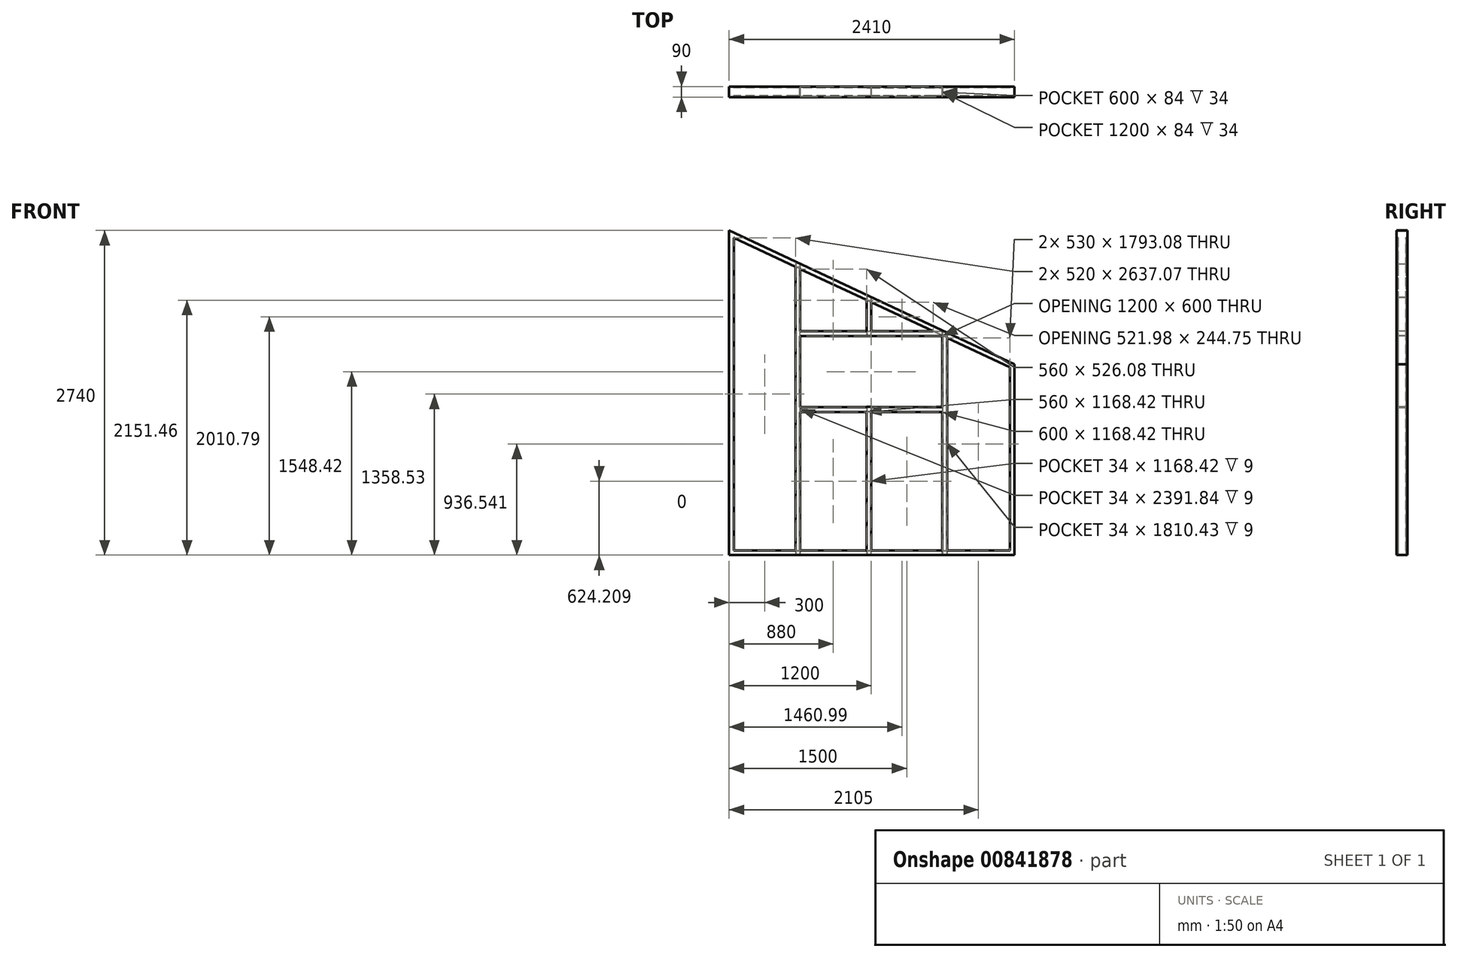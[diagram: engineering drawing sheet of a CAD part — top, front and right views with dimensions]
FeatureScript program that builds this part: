
annotation { "Feature Type Name" : "Feature", "Feature Type Description" : "" }
export const myFeature = defineFeature(function(context is Context, id is Id, definition is map)
    precondition{}
    {
        {
            var Q0;
            Q0=qCreatedBy(makeId("Front.planeOp"),FACE);
            var sketch = newSketch(context, id + "F0", { "sketchPlane" : qUnion([Q0])});
            skLineSegment(sketch, "E0", {"start": v(0, 0) * mm, "end": v(2410, 0) * mm});
            skLineSegment(sketch, "E1", {"start": v(2410, 0) * mm, "end": v(2410, 1610) * mm});
            skLineSegment(sketch, "E2", {"start": v(2410, 1610) * mm, "end": v(0, 2740) * mm});
            skLineSegment(sketch, "E3", {"start": v(0, 2740) * mm, "end": v(0, 0) * mm});
            skSolve(sketch);
        }
        {
            var Q0;
            Q0=qCreatedBy(makeId("Right.planeOp"),FACE);
            var sketch = newSketch(context, id + "F1", { "sketchPlane" : qUnion([Q0])});
            skLineSegment(sketch, "E4", {"start": v(0, 0) * mm, "end": v(-45, 0) * mm});
            skLineSegment(sketch, "E5", {"start": v(-45, 0) * mm, "end": v(-45, 40) * mm});
            skLineSegment(sketch, "E6", {"start": v(-45, 40) * mm, "end": v(-33, 40) * mm});
            skLineSegment(sketch, "E7.MirrorCS", {"start": v(45, 40) * mm, "end": v(33, 40) * mm});
            skLineSegment(sketch, "E8.MirrorCS", {"start": v(45, 0) * mm, "end": v(45, 40) * mm});
            skLineSegment(sketch, "E9.MirrorCS", {"start": v(0, 0) * mm, "end": v(45, 0) * mm});
            skLineSegment(sketch, "E10.0", {"start": v(-42, 37) * mm, "end": v(-33, 37) * mm});
            skLineSegment(sketch, "E10.1", {"start": v(-42, 3) * mm, "end": v(-42, 37) * mm});
            skLineSegment(sketch, "E10.2", {"start": v(42, 37) * mm, "end": v(33, 37) * mm});
            skLineSegment(sketch, "E10.3", {"start": v(42, 3) * mm, "end": v(42, 37) * mm});
            skLineSegment(sketch, "E10.4", {"start": v(0, 3) * mm, "end": v(42, 3) * mm});
            skLineSegment(sketch, "E10.5", {"start": v(0, 3) * mm, "end": v(-42, 3) * mm});
            skLineSegment(sketch, "E11", {"start": v(-33, 40) * mm, "end": v(-33, 37) * mm});
            skLineSegment(sketch, "E12", {"start": v(33, 40) * mm, "end": v(33, 37) * mm});
            skSolve(sketch);
        }
        {
            var Q0;
            Q0=makeQuery(id+"F1.imprint","IMPRINT",FACE,{"disambiguationData":[TD([[makeQuery(id+"F1.imprint","IMPRINT",EDGE,{"derivedFrom":sQuery(id+"F1.wireOp",EDGE,"E4")}),-1.0]])]});
            var Q1;
            Q1=sQuery(id+"F0.wireOp",EDGE,"E0");
            var Q2;
            Q2=sQuery(id+"F0.wireOp",EDGE,"E1");
            var Q3;
            Q3=sQuery(id+"F0.wireOp",EDGE,"E2");
            var Q4;
            Q4=sQuery(id+"F0.wireOp",EDGE,"E3");
            sweep(context, id + "F2", {"profiles" : qUnion([Q0]), "path" : qUnion([Q1, Q2, Q3, Q4])});
        }
        {
            var Q0;
            Q0=qCreatedBy(makeId("Front.planeOp"),FACE);
            var sketch = newSketch(context, id + "F3", { "sketchPlane" : qUnion([Q0])});
            skLineSegment(sketch, "E13", {"start": v(600, 0) * mm, "end": v(600, 2458.67) * mm});
            skLineSegment(sketch, "E14", {"start": v(1200, 0) * mm, "end": v(1200, 1251.84) * mm});
            skLineSegment(sketch, "E15", {"start": v(1800, 0) * mm, "end": v(1800, 1896.02) * mm});
            skLineSegment(sketch, "E16", {"start": v(1800, 1851.84) * mm, "end": v(600, 1851.84) * mm});
            skLineSegment(sketch, "E17", {"start": v(1800, 1251.84) * mm, "end": v(600, 1251.84) * mm});
            skLineSegment(sketch, "E18.trimOffspring", {"start": v(1200, 1851.84) * mm, "end": v(1200, 2177.34) * mm});
            skSolve(sketch);
        }
        {
            var Q0;
            Q0=makeQuery(id+"F2.opSweep","SWEPT_FACE",FACE,{"disambiguationData":[OSD([sQuery(id+"F0.wireOp",EDGE,"E0"),sQuery(id+"F1.wireOp",EDGE,"E4"),sQuery(id+"F1.wireOp",EDGE,"E9.MirrorCS")])]});
            var sketch = newSketch(context, id + "F4", { "sketchPlane" : qUnion([Q0])});
            skLineSegment(sketch, "E19", {"start": v(600, 0) * mm, "end": v(600, 45) * mm});
            skLineSegment(sketch, "E20", {"start": v(600, 45) * mm, "end": v(560, 45) * mm});
            skLineSegment(sketch, "E21", {"start": v(560, 45) * mm, "end": v(560, 33) * mm});
            skLineSegment(sketch, "E22.MirrorCS", {"start": v(600, 0) * mm, "end": v(600, -45) * mm});
            skLineSegment(sketch, "E23.MirrorCS", {"start": v(600, -45) * mm, "end": v(560, -45) * mm});
            skLineSegment(sketch, "E24.MirrorCS", {"start": v(560, -45) * mm, "end": v(560, -33) * mm});
            skLineSegment(sketch, "E25.0", {"start": v(563, -42) * mm, "end": v(563, -33) * mm});
            skLineSegment(sketch, "E25.1", {"start": v(597, -42) * mm, "end": v(563, -42) * mm});
            skLineSegment(sketch, "E25.2", {"start": v(563, 42) * mm, "end": v(563, 33) * mm});
            skLineSegment(sketch, "E25.3", {"start": v(597, 42) * mm, "end": v(563, 42) * mm});
            skLineSegment(sketch, "E25.4", {"start": v(597, 0) * mm, "end": v(597, 42) * mm});
            skLineSegment(sketch, "E25.5", {"start": v(597, 0) * mm, "end": v(597, -42) * mm});
            skLineSegment(sketch, "E26", {"start": v(560, 33) * mm, "end": v(563, 33) * mm});
            skLineSegment(sketch, "E27", {"start": v(560, -33) * mm, "end": v(563, -33) * mm});
            skLineSegment(sketch, "E28.1.0.0", {"start": v(1200, 45) * mm, "end": v(1160, 45) * mm});
            skLineSegment(sketch, "E28.1.0.1", {"start": v(1197, 42) * mm, "end": v(1163, 42) * mm});
            skLineSegment(sketch, "E28.1.0.2", {"start": v(1197, 0) * mm, "end": v(1197, -42) * mm});
            skLineSegment(sketch, "E28.1.0.3", {"start": v(1200, 0) * mm, "end": v(1200, 45) * mm});
            skLineSegment(sketch, "E28.1.0.4", {"start": v(1197, -42) * mm, "end": v(1163, -42) * mm});
            skLineSegment(sketch, "E28.1.0.5", {"start": v(1200, 0) * mm, "end": v(1200, -45) * mm});
            skLineSegment(sketch, "E28.1.0.6", {"start": v(1200, -45) * mm, "end": v(1160, -45) * mm});
            skLineSegment(sketch, "E28.1.0.7", {"start": v(1197, 0) * mm, "end": v(1197, 42) * mm});
            skLineSegment(sketch, "E28.1.0.8", {"start": v(1160, -45) * mm, "end": v(1160, -33) * mm});
            skLineSegment(sketch, "E28.1.0.9", {"start": v(1160, 33) * mm, "end": v(1163, 33) * mm});
            skLineSegment(sketch, "E28.1.0.10", {"start": v(1160, 45) * mm, "end": v(1160, 33) * mm});
            skLineSegment(sketch, "E28.1.0.11", {"start": v(1163, 42) * mm, "end": v(1163, 33) * mm});
            skLineSegment(sketch, "E28.1.0.12", {"start": v(1160, -33) * mm, "end": v(1163, -33) * mm});
            skLineSegment(sketch, "E28.1.0.13", {"start": v(1163, -42) * mm, "end": v(1163, -33) * mm});
            skLineSegment(sketch, "E28.2.0.3", {"start": v(1800, 0) * mm, "end": v(1800, 45) * mm});
            skLineSegment(sketch, "E28.2.0.5", {"start": v(1800, 0) * mm, "end": v(1800, -45) * mm});
            skLineSegment(sketch, "E28.direction1", {"start": v(560, -45) * mm, "end": v(1160, -45) * mm, "construction": true});
            skLineSegment(sketch, "E29.MirrorCS", {"start": v(1803, 0) * mm, "end": v(1803, -42) * mm});
            skLineSegment(sketch, "E30.MirrorCS", {"start": v(1803, -42) * mm, "end": v(1837, -42) * mm});
            skLineSegment(sketch, "E31.MirrorCS", {"start": v(1800, -45) * mm, "end": v(1840, -45) * mm});
            skLineSegment(sketch, "E32.MirrorCS", {"start": v(1840, -45) * mm, "end": v(1840, -33) * mm});
            skLineSegment(sketch, "E33.MirrorCS", {"start": v(1837, -42) * mm, "end": v(1837, -33) * mm});
            skLineSegment(sketch, "E34.MirrorCS", {"start": v(1840, -33) * mm, "end": v(1837, -33) * mm});
            skLineSegment(sketch, "E35.MirrorCS", {"start": v(1803, 0) * mm, "end": v(1803, 42) * mm});
            skLineSegment(sketch, "E36.MirrorCS", {"start": v(1803, 42) * mm, "end": v(1837, 42) * mm});
            skLineSegment(sketch, "E37.MirrorCS", {"start": v(1800, 45) * mm, "end": v(1840, 45) * mm});
            skLineSegment(sketch, "E38.MirrorCS", {"start": v(1837, 42) * mm, "end": v(1837, 33) * mm});
            skLineSegment(sketch, "E39.MirrorCS", {"start": v(1840, 45) * mm, "end": v(1840, 33) * mm});
            skLineSegment(sketch, "E40.MirrorCS", {"start": v(1840, 33) * mm, "end": v(1837, 33) * mm});
            skPoint(sketch, "E28.2.0.10.start.orphan", {"position": v(1760, 45) * mm});
            skPoint(sketch, "E28.2.0.11.start.orphan", {"position": v(1763, 42) * mm});
            skPoint(sketch, "E28.2.0.7.end.orphan", {"position": v(1797, 42) * mm});
            skPoint(sketch, "E28.2.0.2.start.orphan", {"position": v(1797, 0) * mm});
            skPoint(sketch, "E28.2.0.4.start.orphan", {"position": v(1797, -42) * mm});
            skPoint(sketch, "E28.2.0.6.end.orphan", {"position": v(1760, -45) * mm});
            skPoint(sketch, "E28.2.0.6.start.orphan", {"position": v(1800, -45) * mm});
            skPoint(sketch, "E28.2.0.13.start.orphan", {"position": v(1763, -42) * mm});
            skPoint(sketch, "E28.2.0.8.start.orphan", {"position": v(1760, -45) * mm});
            skPoint(sketch, "E28.2.0.12.end.orphan", {"position": v(1763, -33) * mm});
            skPoint(sketch, "E28.2.0.12.start.orphan", {"position": v(1760, -33) * mm});
            skPoint(sketch, "E28.2.0.9.end.orphan", {"position": v(1763, 33) * mm});
            skPoint(sketch, "E28.2.0.9.start.orphan", {"position": v(1760, 33) * mm});
            skSolve(sketch);
        }
        {
            var Q0;
            Q0 = qSketchRegion(id + "F4", true);
            var Q1;
            Q1=makeQuery(id+"F2.opSweep","SWEPT_FACE",FACE,{"disambiguationData":[OSD([sQuery(id+"F0.wireOp",EDGE,"E2"),sQuery(id+"F1.wireOp",EDGE,"E10.4"),sQuery(id+"F1.wireOp",EDGE,"E10.5")])]});
            extrude(context, id + "F5", {"entities" : qUnion([Q0]), "operationType" : NewBodyOperationType.ADD, "endBound" : BoundingType.UP_TO_SURFACE, "oppositeDirection" : true, "depth" : 25 * mm, "endBoundEntityFace" : qUnion([Q1]), "offsetDistance" : 25 * mm});
        }
        {
            var Q0;
            {var subQ0=sQuery(id+"F3.wireOp",EDGE,"E16");var subQ3=makeQuery(id+"F3.imprint","IMPRINT",VERTEX,{"derivedFrom":subQ0});Q0=makeQuery(id+"F3.imprint","IMPRINT",FACE,{"disambiguationData":[TD([[makeQuery(id+"F3.imprint","IMPRINT",EDGE,{"disambiguationData":[TD([[subQ3,1.0]])],"derivedFrom":subQ0}),1.0]])]});}
            var Q1;
            Q1=sQuery(id+"F3.wireOp",EDGE,"E16");
            var Q2;
            Q2=sQuery(id+"F3.wireOp",EDGE,"E17");
            extrude(context, id + "F6", {"entities" : qUnion([Q0]), "operationType" : NewBodyOperationType.REMOVE, "surfaceEntities" : qUnion([Q1, Q2]), "endBound" : BoundingType.THROUGH_ALL, "oppositeDirection" : true, "depth" : 25 * mm, "offsetDistance" : 25 * mm, "hasSecondDirection" : true, "secondDirectionBound" : SecondDirectionBoundingType.THROUGH_ALL, "secondDirectionOppositeDirection" : false, "secondDirectionDepth" : 25 * mm});
        }
        {
            var Q0;
            Q0=makeQuery(id+"F5.opExtrude","SWEPT_FACE",FACE,{"disambiguationData":[OSD([sQuery(id+"F4.wireOp",EDGE,"E19"),sQuery(id+"F4.wireOp",EDGE,"E22.MirrorCS")])]});
            var sketch = newSketch(context, id + "F7", { "sketchPlane" : qUnion([Q0])});
            skLineSegment(sketch, "E41", {"start": v(0, 1248.42) * mm, "end": v(45, 1248.42) * mm});
            skLineSegment(sketch, "E42", {"start": v(45, 1248.42) * mm, "end": v(45, 1208.42) * mm});
            skLineSegment(sketch, "E43", {"start": v(45, 1208.42) * mm, "end": v(33, 1208.42) * mm});
            skLineSegment(sketch, "E44.MirrorCS", {"start": v(0, 1248.42) * mm, "end": v(-45, 1248.42) * mm});
            skLineSegment(sketch, "E45.MirrorCS", {"start": v(-45, 1248.42) * mm, "end": v(-45, 1208.42) * mm});
            skLineSegment(sketch, "E46.MirrorCS", {"start": v(-45, 1208.42) * mm, "end": v(-33, 1208.42) * mm});
            skLineSegment(sketch, "E47.0", {"start": v(42, 1211.42) * mm, "end": v(33, 1211.42) * mm});
            skLineSegment(sketch, "E47.1", {"start": v(42, 1245.42) * mm, "end": v(42, 1211.42) * mm});
            skLineSegment(sketch, "E47.2", {"start": v(-42, 1211.42) * mm, "end": v(-33, 1211.42) * mm});
            skLineSegment(sketch, "E47.3", {"start": v(-42, 1245.42) * mm, "end": v(-42, 1211.42) * mm});
            skLineSegment(sketch, "E47.4", {"start": v(0, 1245.42) * mm, "end": v(-42, 1245.42) * mm});
            skLineSegment(sketch, "E47.5", {"start": v(0, 1245.42) * mm, "end": v(42, 1245.42) * mm});
            skLineSegment(sketch, "E48", {"start": v(33, 1211.42) * mm, "end": v(33, 1208.42) * mm});
            skLineSegment(sketch, "E49", {"start": v(-33, 1211.42) * mm, "end": v(-33, 1208.42) * mm});
            skLineSegment(sketch, "E50", {"start": v(88.19, 1548.42) * mm, "end": v(-130.2, 1548.42) * mm, "construction": true});
            skLineSegment(sketch, "E51.MirrorCS", {"start": v(42, 1885.42) * mm, "end": v(33, 1885.42) * mm});
            skLineSegment(sketch, "E52.MirrorCS", {"start": v(45, 1888.42) * mm, "end": v(33, 1888.42) * mm});
            skLineSegment(sketch, "E53.MirrorCS", {"start": v(-33, 1885.42) * mm, "end": v(-33, 1888.42) * mm});
            skLineSegment(sketch, "E54.MirrorCS", {"start": v(33, 1885.42) * mm, "end": v(33, 1888.42) * mm});
            skLineSegment(sketch, "E55.MirrorCS", {"start": v(-45, 1888.42) * mm, "end": v(-33, 1888.42) * mm});
            skLineSegment(sketch, "E56.MirrorCS", {"start": v(-42, 1885.42) * mm, "end": v(-33, 1885.42) * mm});
            skLineSegment(sketch, "E57.MirrorCS", {"start": v(45, 1848.42) * mm, "end": v(45, 1888.42) * mm});
            skLineSegment(sketch, "E58.MirrorCS", {"start": v(42, 1851.42) * mm, "end": v(42, 1885.42) * mm});
            skLineSegment(sketch, "E59.MirrorCS", {"start": v(0, 1851.42) * mm, "end": v(-42, 1851.42) * mm});
            skLineSegment(sketch, "E60.MirrorCS", {"start": v(-42, 1851.42) * mm, "end": v(-42, 1885.42) * mm});
            skLineSegment(sketch, "E61.MirrorCS", {"start": v(-45, 1848.42) * mm, "end": v(-45, 1888.42) * mm});
            skLineSegment(sketch, "E62.MirrorCS", {"start": v(0, 1848.42) * mm, "end": v(-45, 1848.42) * mm});
            skLineSegment(sketch, "E63.MirrorCS", {"start": v(0, 1851.42) * mm, "end": v(42, 1851.42) * mm});
            skLineSegment(sketch, "E64.MirrorCS", {"start": v(0, 1848.42) * mm, "end": v(45, 1848.42) * mm});
            skSolve(sketch);
        }
        {
            var Q0;
            Q0 = qSketchRegion(id + "F7", true);
            var Q1;
            Q1=makeQuery(id+"F5.opExtrude","SWEPT_FACE",FACE,{"disambiguationData":[OSD([sQuery(id+"F4.wireOp",EDGE,"E28.2.0.3"),sQuery(id+"F4.wireOp",EDGE,"E28.2.0.5")])]});
            extrude(context, id + "F8", {"entities" : qUnion([Q0]), "operationType" : NewBodyOperationType.ADD, "endBound" : BoundingType.UP_TO_SURFACE, "depth" : 25 * mm, "endBoundEntityFace" : qUnion([Q1]), "offsetDistance" : 25 * mm});
        }
    });
